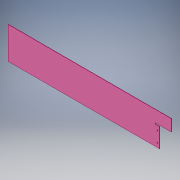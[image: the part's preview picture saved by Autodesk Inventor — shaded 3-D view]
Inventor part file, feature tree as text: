
AUTODESK INVENTOR PART (.ipt)
format: ipt  version: 2018 (Build 220112000, 112)  size: 117,760 bytes
history: native  units: mm
features: extrude x3, sketch x3
ambient origin geometry x8: Origin, YZ Plane, XZ Plane, XY Plane, X Axis, Y Axis, Z Axis, Center Point
bodies: Solid1 (feature_tree)
feature tree (6):
  extrude  "Extrusion1"  Depth=150.0mm
  extrude  "Extrusion3"  Depth=20.0mm
  extrude  "Extrusion4"  Depth=75.0mm
  sketch  "Sketch1"  dims[d0=710.0mm d1=150.0mm]
  sketch  "Sketch2"  dims[d2=1.6mm d3=0.0mm d6=20.0mm]
  sketch  "Sketch3"  dims[d7=60.0mm d10=5.0mm d11=5.0mm d12=50.0mm d13=20.0mm d14=1.6mm d15=0.0mm d16=54.0mm d17=1.6mm d18=75.0mm d19=0.0mm]
